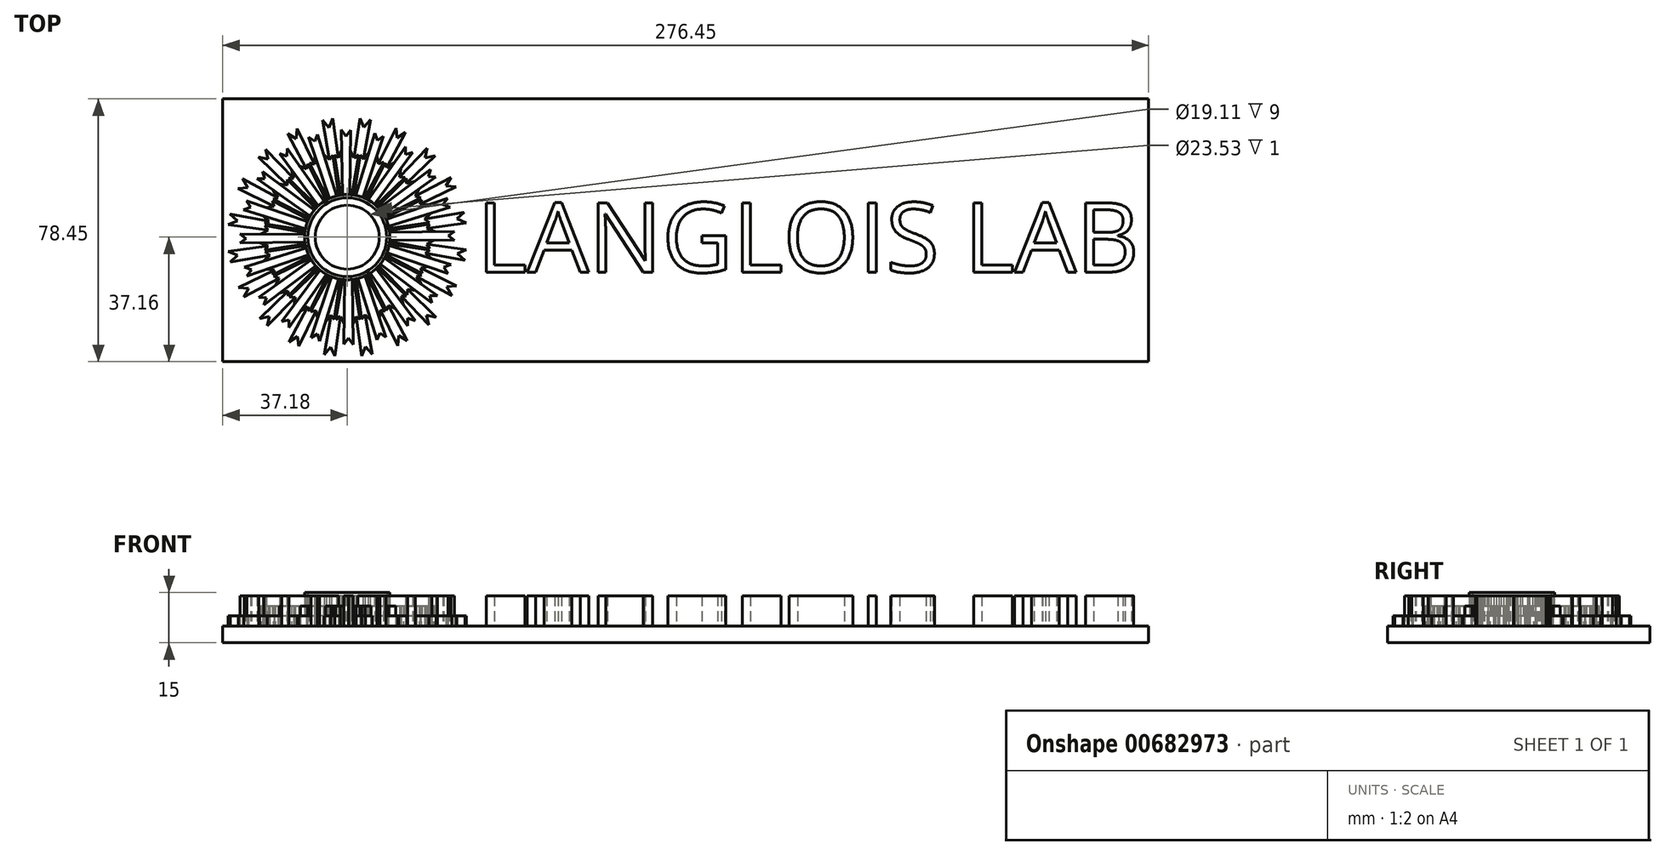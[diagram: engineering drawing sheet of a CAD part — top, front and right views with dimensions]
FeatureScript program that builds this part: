
annotation { "Feature Type Name" : "Feature", "Feature Type Description" : "" }
export const myFeature = defineFeature(function(context is Context, id is Id, definition is map)
    precondition{}
    {
        {
            var Q0;
            Q0=qCreatedBy(makeId("Top.planeOp"),FACE);
            var sketch = newSketch(context, id + "F0", { "sketchPlane" : qUnion([Q0])});
            skCircle(sketch, "E0", {"center": v(0, 0) * mm, "radius": 9.55 * mm});
            skCircle(sketch, "E1", {"center": v(0, 0) * mm, "radius": 11.77 * mm});
            skCircle(sketch, "E2", {"center": v(0, 0) * mm, "radius": 12.74 * mm});
            skLineSegment(sketch, "E3", {"start": v(-8.1, -9.83) * mm, "end": v(-19.6, -25.28) * mm});
            skLineSegment(sketch, "E4", {"start": v(-19.6, -25.28) * mm, "end": v(-17.42, -24.67) * mm});
            skLineSegment(sketch, "E5", {"start": v(-17.42, -24.67) * mm, "end": v(-17.42, -26.96) * mm});
            skLineSegment(sketch, "E6", {"start": v(-17.42, -26.96) * mm, "end": v(-6.24, -11.1) * mm});
            skLineSegment(sketch, "E7.1.0", {"start": v(-8.24, -31.02) * mm, "end": v(-2.5, -12.49) * mm});
            skLineSegment(sketch, "E7.1.1", {"start": v(-8.95, -28.84) * mm, "end": v(-8.24, -31.02) * mm});
            skLineSegment(sketch, "E7.1.2", {"start": v(-10.83, -30.1) * mm, "end": v(-8.95, -28.84) * mm});
            skLineSegment(sketch, "E7.1.3", {"start": v(-4.67, -11.85) * mm, "end": v(-10.83, -30.1) * mm});
            skLineSegment(sketch, "E7.2.0", {"start": v(1.75, -32.05) * mm, "end": v(1.47, -12.65) * mm});
            skLineSegment(sketch, "E7.2.1", {"start": v(0.4, -30.2) * mm, "end": v(1.75, -32.05) * mm});
            skLineSegment(sketch, "E7.2.2", {"start": v(-1, -31.97) * mm, "end": v(0.4, -30.2) * mm});
            skLineSegment(sketch, "E7.2.3", {"start": v(-0.77, -12.71) * mm, "end": v(-1, -31.97) * mm});
            skLineSegment(sketch, "E7.3.0", {"start": v(11.57, -29.94) * mm, "end": v(5.31, -11.58) * mm});
            skLineSegment(sketch, "E7.3.1", {"start": v(9.71, -28.6) * mm, "end": v(11.57, -29.94) * mm});
            skLineSegment(sketch, "E7.3.2", {"start": v(8.93, -30.71) * mm, "end": v(9.71, -28.6) * mm});
            skLineSegment(sketch, "E7.3.3", {"start": v(3.2, -12.33) * mm, "end": v(8.93, -30.71) * mm});
            skLineSegment(sketch, "E7.4.0", {"start": v(20.25, -24.9) * mm, "end": v(8.63, -9.37) * mm});
            skLineSegment(sketch, "E7.4.1", {"start": v(18.08, -24.2) * mm, "end": v(20.25, -24.9) * mm});
            skLineSegment(sketch, "E7.4.2", {"start": v(17.98, -26.45) * mm, "end": v(18.08, -24.2) * mm});
            skLineSegment(sketch, "E7.4.3", {"start": v(6.85, -10.74) * mm, "end": v(17.98, -26.45) * mm});
            skLineSegment(sketch, "E7.5.0", {"start": v(26.96, -17.42) * mm, "end": v(11.1, -6.24) * mm});
            skLineSegment(sketch, "E7.5.1", {"start": v(24.67, -17.42) * mm, "end": v(26.96, -17.42) * mm});
            skLineSegment(sketch, "E7.5.2", {"start": v(25.28, -19.6) * mm, "end": v(24.67, -17.42) * mm});
            skLineSegment(sketch, "E7.5.3", {"start": v(9.83, -8.1) * mm, "end": v(25.28, -19.6) * mm});
            skLineSegment(sketch, "E7.6.0", {"start": v(31.02, -8.24) * mm, "end": v(12.49, -2.5) * mm});
            skLineSegment(sketch, "E7.6.1", {"start": v(28.84, -8.95) * mm, "end": v(31.02, -8.24) * mm});
            skLineSegment(sketch, "E7.6.2", {"start": v(30.1, -10.83) * mm, "end": v(28.84, -8.95) * mm});
            skLineSegment(sketch, "E7.6.3", {"start": v(11.85, -4.67) * mm, "end": v(30.1, -10.83) * mm});
            skLineSegment(sketch, "E7.7.0", {"start": v(32.05, 1.75) * mm, "end": v(12.65, 1.47) * mm});
            skLineSegment(sketch, "E7.7.1", {"start": v(30.2, 0.4) * mm, "end": v(32.05, 1.75) * mm});
            skLineSegment(sketch, "E7.7.2", {"start": v(31.97, -1) * mm, "end": v(30.2, 0.4) * mm});
            skLineSegment(sketch, "E7.7.3", {"start": v(12.71, -0.77) * mm, "end": v(31.97, -1) * mm});
            skLineSegment(sketch, "E7.8.0", {"start": v(29.94, 11.57) * mm, "end": v(11.58, 5.31) * mm});
            skLineSegment(sketch, "E7.8.1", {"start": v(28.6, 9.71) * mm, "end": v(29.94, 11.57) * mm});
            skLineSegment(sketch, "E7.8.2", {"start": v(30.71, 8.93) * mm, "end": v(28.6, 9.71) * mm});
            skLineSegment(sketch, "E7.8.3", {"start": v(12.33, 3.2) * mm, "end": v(30.71, 8.93) * mm});
            skLineSegment(sketch, "E7.9.0", {"start": v(24.9, 20.25) * mm, "end": v(9.37, 8.63) * mm});
            skLineSegment(sketch, "E7.9.1", {"start": v(24.2, 18.08) * mm, "end": v(24.9, 20.25) * mm});
            skLineSegment(sketch, "E7.9.2", {"start": v(26.45, 17.98) * mm, "end": v(24.2, 18.08) * mm});
            skLineSegment(sketch, "E7.9.3", {"start": v(10.74, 6.85) * mm, "end": v(26.45, 17.98) * mm});
            skLineSegment(sketch, "E7.10.0", {"start": v(17.42, 26.96) * mm, "end": v(6.24, 11.1) * mm});
            skLineSegment(sketch, "E7.10.1", {"start": v(17.42, 24.67) * mm, "end": v(17.42, 26.96) * mm});
            skLineSegment(sketch, "E7.10.2", {"start": v(19.6, 25.28) * mm, "end": v(17.42, 24.67) * mm});
            skLineSegment(sketch, "E7.10.3", {"start": v(8.1, 9.83) * mm, "end": v(19.6, 25.28) * mm});
            skLineSegment(sketch, "E7.11.0", {"start": v(8.24, 31.02) * mm, "end": v(2.5, 12.49) * mm});
            skLineSegment(sketch, "E7.11.1", {"start": v(8.95, 28.84) * mm, "end": v(8.24, 31.02) * mm});
            skLineSegment(sketch, "E7.11.2", {"start": v(10.83, 30.1) * mm, "end": v(8.95, 28.84) * mm});
            skLineSegment(sketch, "E7.11.3", {"start": v(4.67, 11.85) * mm, "end": v(10.83, 30.1) * mm});
            skLineSegment(sketch, "E7.12.0", {"start": v(-1.75, 32.05) * mm, "end": v(-1.47, 12.65) * mm});
            skLineSegment(sketch, "E7.12.1", {"start": v(-0.4, 30.2) * mm, "end": v(-1.75, 32.05) * mm});
            skLineSegment(sketch, "E7.12.2", {"start": v(1, 31.97) * mm, "end": v(-0.4, 30.2) * mm});
            skLineSegment(sketch, "E7.12.3", {"start": v(0.77, 12.71) * mm, "end": v(1, 31.97) * mm});
            skLineSegment(sketch, "E7.13.0", {"start": v(-11.57, 29.94) * mm, "end": v(-5.31, 11.58) * mm});
            skLineSegment(sketch, "E7.13.1", {"start": v(-9.71, 28.6) * mm, "end": v(-11.57, 29.94) * mm});
            skLineSegment(sketch, "E7.13.2", {"start": v(-8.93, 30.71) * mm, "end": v(-9.71, 28.6) * mm});
            skLineSegment(sketch, "E7.13.3", {"start": v(-3.2, 12.33) * mm, "end": v(-8.93, 30.71) * mm});
            skLineSegment(sketch, "E7.14.0", {"start": v(-20.25, 24.9) * mm, "end": v(-8.63, 9.37) * mm});
            skLineSegment(sketch, "E7.14.1", {"start": v(-18.08, 24.2) * mm, "end": v(-20.25, 24.9) * mm});
            skLineSegment(sketch, "E7.14.2", {"start": v(-17.98, 26.45) * mm, "end": v(-18.08, 24.2) * mm});
            skLineSegment(sketch, "E7.14.3", {"start": v(-6.85, 10.74) * mm, "end": v(-17.98, 26.45) * mm});
            skLineSegment(sketch, "E7.15.0", {"start": v(-26.96, 17.42) * mm, "end": v(-11.1, 6.24) * mm});
            skLineSegment(sketch, "E7.15.1", {"start": v(-24.67, 17.42) * mm, "end": v(-26.96, 17.42) * mm});
            skLineSegment(sketch, "E7.15.2", {"start": v(-25.28, 19.6) * mm, "end": v(-24.67, 17.42) * mm});
            skLineSegment(sketch, "E7.15.3", {"start": v(-9.83, 8.1) * mm, "end": v(-25.28, 19.6) * mm});
            skLineSegment(sketch, "E7.16.0", {"start": v(-31.02, 8.24) * mm, "end": v(-12.49, 2.5) * mm});
            skLineSegment(sketch, "E7.16.1", {"start": v(-28.84, 8.95) * mm, "end": v(-31.02, 8.24) * mm});
            skLineSegment(sketch, "E7.16.2", {"start": v(-30.1, 10.83) * mm, "end": v(-28.84, 8.95) * mm});
            skLineSegment(sketch, "E7.16.3", {"start": v(-11.85, 4.67) * mm, "end": v(-30.1, 10.83) * mm});
            skLineSegment(sketch, "E7.17.0", {"start": v(-32.05, -1.75) * mm, "end": v(-12.65, -1.47) * mm});
            skLineSegment(sketch, "E7.17.1", {"start": v(-30.2, -0.4) * mm, "end": v(-32.05, -1.75) * mm});
            skLineSegment(sketch, "E7.17.2", {"start": v(-31.97, 1) * mm, "end": v(-30.2, -0.4) * mm});
            skLineSegment(sketch, "E7.17.3", {"start": v(-12.71, 0.77) * mm, "end": v(-31.97, 1) * mm});
            skLineSegment(sketch, "E7.18.0", {"start": v(-29.94, -11.57) * mm, "end": v(-11.58, -5.31) * mm});
            skLineSegment(sketch, "E7.18.1", {"start": v(-28.6, -9.71) * mm, "end": v(-29.94, -11.57) * mm});
            skLineSegment(sketch, "E7.18.2", {"start": v(-30.71, -8.93) * mm, "end": v(-28.6, -9.71) * mm});
            skLineSegment(sketch, "E7.18.3", {"start": v(-12.33, -3.2) * mm, "end": v(-30.71, -8.93) * mm});
            skLineSegment(sketch, "E7.19.0", {"start": v(-24.9, -20.25) * mm, "end": v(-9.37, -8.63) * mm});
            skLineSegment(sketch, "E7.19.1", {"start": v(-24.2, -18.08) * mm, "end": v(-24.9, -20.25) * mm});
            skLineSegment(sketch, "E7.19.2", {"start": v(-26.45, -17.98) * mm, "end": v(-24.2, -18.08) * mm});
            skLineSegment(sketch, "E7.19.3", {"start": v(-10.74, -6.85) * mm, "end": v(-26.45, -17.98) * mm});
            skLineSegment(sketch, "E8", {"start": v(-14, -22.1) * mm, "end": v(-11.8, -20.73) * mm});
            skLineSegment(sketch, "E9", {"start": v(-11.8, -20.73) * mm, "end": v(-11.35, -22.17) * mm});
            skLineSegment(sketch, "E10", {"start": v(-11.35, -22.17) * mm, "end": v(-5.84, -11.32) * mm});
            skLineSegment(sketch, "E11", {"start": v(-5.22, -11.62) * mm, "end": v(-10.89, -22.36) * mm});
            skLineSegment(sketch, "E12", {"start": v(-10.89, -22.36) * mm, "end": v(-9.26, -21.9) * mm});
            skLineSegment(sketch, "E13", {"start": v(-9.26, -21.9) * mm, "end": v(-8.86, -24.28) * mm});
            skLineSegment(sketch, "E14", {"start": v(-11.8, -20.73) * mm, "end": v(-17.42, -31.26) * mm});
            skLineSegment(sketch, "E15", {"start": v(-17.42, -31.26) * mm, "end": v(-14.82, -29.7) * mm});
            skLineSegment(sketch, "E16", {"start": v(-14.82, -29.7) * mm, "end": v(-14.53, -32.63) * mm});
            skLineSegment(sketch, "E17", {"start": v(-14.53, -32.63) * mm, "end": v(-9.26, -21.9) * mm});
            skLineSegment(sketch, "E18.1.0", {"start": v(-6.49, -25.35) * mm, "end": v(-4.81, -23.36) * mm});
            skLineSegment(sketch, "E18.1.1", {"start": v(-4.81, -23.36) * mm, "end": v(-6.91, -35.11) * mm});
            skLineSegment(sketch, "E18.1.2", {"start": v(-4.81, -23.36) * mm, "end": v(-3.94, -24.6) * mm});
            skLineSegment(sketch, "E18.1.3", {"start": v(-3.94, -24.6) * mm, "end": v(-2.05, -12.57) * mm});
            skLineSegment(sketch, "E18.1.4", {"start": v(-3.74, -35.52) * mm, "end": v(-2.04, -23.68) * mm});
            skLineSegment(sketch, "E18.1.5", {"start": v(-3.45, -24.63) * mm, "end": v(-2.04, -23.68) * mm});
            skLineSegment(sketch, "E18.1.6", {"start": v(-1.37, -12.66) * mm, "end": v(-3.45, -24.63) * mm});
            skLineSegment(sketch, "E18.1.7", {"start": v(-2.04, -23.68) * mm, "end": v(-0.93, -25.83) * mm});
            skLineSegment(sketch, "E18.1.8", {"start": v(-4.92, -32.82) * mm, "end": v(-3.74, -35.52) * mm});
            skLineSegment(sketch, "E18.1.9", {"start": v(-6.91, -35.11) * mm, "end": v(-4.92, -32.82) * mm});
            skLineSegment(sketch, "E18.2.0", {"start": v(1.67, -26.11) * mm, "end": v(2.64, -23.7) * mm});
            skLineSegment(sketch, "E18.2.1", {"start": v(2.64, -23.7) * mm, "end": v(4.28, -35.53) * mm});
            skLineSegment(sketch, "E18.2.2", {"start": v(2.64, -23.7) * mm, "end": v(3.85, -24.6) * mm});
            skLineSegment(sketch, "E18.2.3", {"start": v(3.85, -24.6) * mm, "end": v(1.93, -12.59) * mm});
            skLineSegment(sketch, "E18.2.4", {"start": v(7.42, -34.94) * mm, "end": v(5.38, -23.16) * mm});
            skLineSegment(sketch, "E18.2.5", {"start": v(4.33, -24.49) * mm, "end": v(5.38, -23.16) * mm});
            skLineSegment(sketch, "E18.2.6", {"start": v(2.6, -12.47) * mm, "end": v(4.33, -24.49) * mm});
            skLineSegment(sketch, "E18.2.7", {"start": v(5.38, -23.16) * mm, "end": v(7.1, -24.85) * mm});
            skLineSegment(sketch, "E18.2.8", {"start": v(5.47, -32.74) * mm, "end": v(7.42, -34.94) * mm});
            skLineSegment(sketch, "E18.2.9", {"start": v(4.28, -35.53) * mm, "end": v(5.47, -32.74) * mm});
            skLineSegment(sketch, "E18.3.0", {"start": v(9.65, -24.32) * mm, "end": v(9.84, -21.72) * mm});
            skLineSegment(sketch, "E18.3.1", {"start": v(9.84, -21.72) * mm, "end": v(15.05, -32.47) * mm});
            skLineSegment(sketch, "E18.3.2", {"start": v(9.84, -21.72) * mm, "end": v(11.27, -22.21) * mm});
            skLineSegment(sketch, "E18.3.3", {"start": v(11.27, -22.21) * mm, "end": v(5.73, -11.38) * mm});
            skLineSegment(sketch, "E18.3.4", {"start": v(17.85, -30.93) * mm, "end": v(12.27, -20.36) * mm});
            skLineSegment(sketch, "E18.3.5", {"start": v(11.69, -21.95) * mm, "end": v(12.27, -20.36) * mm});
            skLineSegment(sketch, "E18.3.6", {"start": v(6.33, -11.05) * mm, "end": v(11.69, -21.95) * mm});
            skLineSegment(sketch, "E18.3.7", {"start": v(12.27, -20.36) * mm, "end": v(14.43, -21.44) * mm});
            skLineSegment(sketch, "E18.3.8", {"start": v(15.31, -29.45) * mm, "end": v(17.85, -30.93) * mm});
            skLineSegment(sketch, "E18.3.9", {"start": v(15.05, -32.47) * mm, "end": v(15.31, -29.45) * mm});
            skLineSegment(sketch, "E18.4.0", {"start": v(16.7, -20.15) * mm, "end": v(16.07, -17.62) * mm});
            skLineSegment(sketch, "E18.4.1", {"start": v(16.07, -17.62) * mm, "end": v(24.34, -26.23) * mm});
            skLineSegment(sketch, "E18.4.2", {"start": v(16.07, -17.62) * mm, "end": v(17.58, -17.64) * mm});
            skLineSegment(sketch, "E18.4.3", {"start": v(17.58, -17.64) * mm, "end": v(8.96, -9.05) * mm});
            skLineSegment(sketch, "E18.4.4", {"start": v(26.54, -23.9) * mm, "end": v(17.96, -15.57) * mm});
            skLineSegment(sketch, "E18.4.5", {"start": v(17.9, -17.27) * mm, "end": v(17.96, -15.57) * mm});
            skLineSegment(sketch, "E18.4.6", {"start": v(9.44, -8.55) * mm, "end": v(17.9, -17.27) * mm});
            skLineSegment(sketch, "E18.4.7", {"start": v(17.96, -15.57) * mm, "end": v(20.35, -15.93) * mm});
            skLineSegment(sketch, "E18.4.8", {"start": v(23.66, -23.27) * mm, "end": v(26.54, -23.9) * mm});
            skLineSegment(sketch, "E18.4.9", {"start": v(24.34, -26.23) * mm, "end": v(23.66, -23.27) * mm});
            skLineSegment(sketch, "E18.5.0", {"start": v(22.1, -14) * mm, "end": v(20.73, -11.8) * mm});
            skLineSegment(sketch, "E18.5.1", {"start": v(20.73, -11.8) * mm, "end": v(31.26, -17.42) * mm});
            skLineSegment(sketch, "E18.5.2", {"start": v(20.73, -11.8) * mm, "end": v(22.17, -11.35) * mm});
            skLineSegment(sketch, "E18.5.3", {"start": v(22.17, -11.35) * mm, "end": v(11.32, -5.84) * mm});
            skLineSegment(sketch, "E18.5.4", {"start": v(32.63, -14.53) * mm, "end": v(21.9, -9.26) * mm});
            skLineSegment(sketch, "E18.5.5", {"start": v(22.36, -10.89) * mm, "end": v(21.9, -9.26) * mm});
            skLineSegment(sketch, "E18.5.6", {"start": v(11.62, -5.22) * mm, "end": v(22.36, -10.89) * mm});
            skLineSegment(sketch, "E18.5.7", {"start": v(21.9, -9.26) * mm, "end": v(24.28, -8.86) * mm});
            skLineSegment(sketch, "E18.5.8", {"start": v(29.7, -14.82) * mm, "end": v(32.63, -14.53) * mm});
            skLineSegment(sketch, "E18.5.9", {"start": v(31.26, -17.42) * mm, "end": v(29.7, -14.82) * mm});
            skLineSegment(sketch, "E18.6.0", {"start": v(25.35, -6.49) * mm, "end": v(23.36, -4.81) * mm});
            skLineSegment(sketch, "E18.6.1", {"start": v(23.36, -4.81) * mm, "end": v(35.11, -6.91) * mm});
            skLineSegment(sketch, "E18.6.2", {"start": v(23.36, -4.81) * mm, "end": v(24.6, -3.94) * mm});
            skLineSegment(sketch, "E18.6.3", {"start": v(24.6, -3.94) * mm, "end": v(12.57, -2.05) * mm});
            skLineSegment(sketch, "E18.6.4", {"start": v(35.52, -3.74) * mm, "end": v(23.68, -2.04) * mm});
            skLineSegment(sketch, "E18.6.5", {"start": v(24.63, -3.45) * mm, "end": v(23.68, -2.04) * mm});
            skLineSegment(sketch, "E18.6.6", {"start": v(12.66, -1.37) * mm, "end": v(24.63, -3.45) * mm});
            skLineSegment(sketch, "E18.6.7", {"start": v(23.68, -2.04) * mm, "end": v(25.83, -0.93) * mm});
            skLineSegment(sketch, "E18.6.8", {"start": v(32.82, -4.92) * mm, "end": v(35.52, -3.74) * mm});
            skLineSegment(sketch, "E18.6.9", {"start": v(35.11, -6.91) * mm, "end": v(32.82, -4.92) * mm});
            skLineSegment(sketch, "E18.7.0", {"start": v(26.11, 1.67) * mm, "end": v(23.7, 2.64) * mm});
            skLineSegment(sketch, "E18.7.1", {"start": v(23.7, 2.64) * mm, "end": v(35.53, 4.28) * mm});
            skLineSegment(sketch, "E18.7.2", {"start": v(23.7, 2.64) * mm, "end": v(24.6, 3.85) * mm});
            skLineSegment(sketch, "E18.7.3", {"start": v(24.6, 3.85) * mm, "end": v(12.59, 1.93) * mm});
            skLineSegment(sketch, "E18.7.4", {"start": v(34.94, 7.42) * mm, "end": v(23.16, 5.38) * mm});
            skLineSegment(sketch, "E18.7.5", {"start": v(24.49, 4.33) * mm, "end": v(23.16, 5.38) * mm});
            skLineSegment(sketch, "E18.7.6", {"start": v(12.47, 2.6) * mm, "end": v(24.49, 4.33) * mm});
            skLineSegment(sketch, "E18.7.7", {"start": v(23.16, 5.38) * mm, "end": v(24.85, 7.1) * mm});
            skLineSegment(sketch, "E18.7.8", {"start": v(32.74, 5.47) * mm, "end": v(34.94, 7.42) * mm});
            skLineSegment(sketch, "E18.7.9", {"start": v(35.53, 4.28) * mm, "end": v(32.74, 5.47) * mm});
            skLineSegment(sketch, "E18.8.0", {"start": v(24.32, 9.65) * mm, "end": v(21.72, 9.84) * mm});
            skLineSegment(sketch, "E18.8.1", {"start": v(21.72, 9.84) * mm, "end": v(32.47, 15.05) * mm});
            skLineSegment(sketch, "E18.8.2", {"start": v(21.72, 9.84) * mm, "end": v(22.21, 11.27) * mm});
            skLineSegment(sketch, "E18.8.3", {"start": v(22.21, 11.27) * mm, "end": v(11.38, 5.73) * mm});
            skLineSegment(sketch, "E18.8.4", {"start": v(30.93, 17.85) * mm, "end": v(20.36, 12.27) * mm});
            skLineSegment(sketch, "E18.8.5", {"start": v(21.95, 11.69) * mm, "end": v(20.36, 12.27) * mm});
            skLineSegment(sketch, "E18.8.6", {"start": v(11.05, 6.33) * mm, "end": v(21.95, 11.69) * mm});
            skLineSegment(sketch, "E18.8.7", {"start": v(20.36, 12.27) * mm, "end": v(21.44, 14.43) * mm});
            skLineSegment(sketch, "E18.8.8", {"start": v(29.45, 15.31) * mm, "end": v(30.93, 17.85) * mm});
            skLineSegment(sketch, "E18.8.9", {"start": v(32.47, 15.05) * mm, "end": v(29.45, 15.31) * mm});
            skLineSegment(sketch, "E18.9.0", {"start": v(20.15, 16.7) * mm, "end": v(17.62, 16.07) * mm});
            skLineSegment(sketch, "E18.9.1", {"start": v(17.62, 16.07) * mm, "end": v(26.23, 24.34) * mm});
            skLineSegment(sketch, "E18.9.2", {"start": v(17.62, 16.07) * mm, "end": v(17.64, 17.58) * mm});
            skLineSegment(sketch, "E18.9.3", {"start": v(17.64, 17.58) * mm, "end": v(9.05, 8.96) * mm});
            skLineSegment(sketch, "E18.9.4", {"start": v(23.9, 26.54) * mm, "end": v(15.57, 17.96) * mm});
            skLineSegment(sketch, "E18.9.5", {"start": v(17.27, 17.9) * mm, "end": v(15.57, 17.96) * mm});
            skLineSegment(sketch, "E18.9.6", {"start": v(8.55, 9.44) * mm, "end": v(17.27, 17.9) * mm});
            skLineSegment(sketch, "E18.9.7", {"start": v(15.57, 17.96) * mm, "end": v(15.93, 20.35) * mm});
            skLineSegment(sketch, "E18.9.8", {"start": v(23.27, 23.66) * mm, "end": v(23.9, 26.54) * mm});
            skLineSegment(sketch, "E18.9.9", {"start": v(26.23, 24.34) * mm, "end": v(23.27, 23.66) * mm});
            skLineSegment(sketch, "E18.10.0", {"start": v(14, 22.1) * mm, "end": v(11.8, 20.73) * mm});
            skLineSegment(sketch, "E18.10.1", {"start": v(11.8, 20.73) * mm, "end": v(17.42, 31.26) * mm});
            skLineSegment(sketch, "E18.10.2", {"start": v(11.8, 20.73) * mm, "end": v(11.35, 22.17) * mm});
            skLineSegment(sketch, "E18.10.3", {"start": v(11.35, 22.17) * mm, "end": v(5.84, 11.32) * mm});
            skLineSegment(sketch, "E18.10.4", {"start": v(14.53, 32.63) * mm, "end": v(9.26, 21.9) * mm});
            skLineSegment(sketch, "E18.10.5", {"start": v(10.89, 22.36) * mm, "end": v(9.26, 21.9) * mm});
            skLineSegment(sketch, "E18.10.6", {"start": v(5.22, 11.62) * mm, "end": v(10.89, 22.36) * mm});
            skLineSegment(sketch, "E18.10.7", {"start": v(9.26, 21.9) * mm, "end": v(8.86, 24.28) * mm});
            skLineSegment(sketch, "E18.10.8", {"start": v(14.82, 29.7) * mm, "end": v(14.53, 32.63) * mm});
            skLineSegment(sketch, "E18.10.9", {"start": v(17.42, 31.26) * mm, "end": v(14.82, 29.7) * mm});
            skLineSegment(sketch, "E18.11.0", {"start": v(6.49, 25.35) * mm, "end": v(4.81, 23.36) * mm});
            skLineSegment(sketch, "E18.11.1", {"start": v(4.81, 23.36) * mm, "end": v(6.91, 35.11) * mm});
            skLineSegment(sketch, "E18.11.2", {"start": v(4.81, 23.36) * mm, "end": v(3.94, 24.6) * mm});
            skLineSegment(sketch, "E18.11.3", {"start": v(3.94, 24.6) * mm, "end": v(2.05, 12.57) * mm});
            skLineSegment(sketch, "E18.11.4", {"start": v(3.74, 35.52) * mm, "end": v(2.04, 23.68) * mm});
            skLineSegment(sketch, "E18.11.5", {"start": v(3.45, 24.63) * mm, "end": v(2.04, 23.68) * mm});
            skLineSegment(sketch, "E18.11.6", {"start": v(1.37, 12.66) * mm, "end": v(3.45, 24.63) * mm});
            skLineSegment(sketch, "E18.11.7", {"start": v(2.04, 23.68) * mm, "end": v(0.93, 25.83) * mm});
            skLineSegment(sketch, "E18.11.8", {"start": v(4.92, 32.82) * mm, "end": v(3.74, 35.52) * mm});
            skLineSegment(sketch, "E18.11.9", {"start": v(6.91, 35.11) * mm, "end": v(4.92, 32.82) * mm});
            skLineSegment(sketch, "E18.12.0", {"start": v(-1.67, 26.11) * mm, "end": v(-2.64, 23.7) * mm});
            skLineSegment(sketch, "E18.12.1", {"start": v(-2.64, 23.7) * mm, "end": v(-4.28, 35.53) * mm});
            skLineSegment(sketch, "E18.12.2", {"start": v(-2.64, 23.7) * mm, "end": v(-3.85, 24.6) * mm});
            skLineSegment(sketch, "E18.12.3", {"start": v(-3.85, 24.6) * mm, "end": v(-1.93, 12.59) * mm});
            skLineSegment(sketch, "E18.12.4", {"start": v(-7.42, 34.94) * mm, "end": v(-5.38, 23.16) * mm});
            skLineSegment(sketch, "E18.12.5", {"start": v(-4.33, 24.49) * mm, "end": v(-5.38, 23.16) * mm});
            skLineSegment(sketch, "E18.12.6", {"start": v(-2.6, 12.47) * mm, "end": v(-4.33, 24.49) * mm});
            skLineSegment(sketch, "E18.12.7", {"start": v(-5.38, 23.16) * mm, "end": v(-7.1, 24.85) * mm});
            skLineSegment(sketch, "E18.12.8", {"start": v(-5.47, 32.74) * mm, "end": v(-7.42, 34.94) * mm});
            skLineSegment(sketch, "E18.12.9", {"start": v(-4.28, 35.53) * mm, "end": v(-5.47, 32.74) * mm});
            skLineSegment(sketch, "E18.13.0", {"start": v(-9.65, 24.32) * mm, "end": v(-9.84, 21.72) * mm});
            skLineSegment(sketch, "E18.13.1", {"start": v(-9.84, 21.72) * mm, "end": v(-15.05, 32.47) * mm});
            skLineSegment(sketch, "E18.13.2", {"start": v(-9.84, 21.72) * mm, "end": v(-11.27, 22.21) * mm});
            skLineSegment(sketch, "E18.13.3", {"start": v(-11.27, 22.21) * mm, "end": v(-5.73, 11.38) * mm});
            skLineSegment(sketch, "E18.13.4", {"start": v(-17.85, 30.93) * mm, "end": v(-12.27, 20.36) * mm});
            skLineSegment(sketch, "E18.13.5", {"start": v(-11.69, 21.95) * mm, "end": v(-12.27, 20.36) * mm});
            skLineSegment(sketch, "E18.13.6", {"start": v(-6.33, 11.05) * mm, "end": v(-11.69, 21.95) * mm});
            skLineSegment(sketch, "E18.13.7", {"start": v(-12.27, 20.36) * mm, "end": v(-14.43, 21.44) * mm});
            skLineSegment(sketch, "E18.13.8", {"start": v(-15.31, 29.45) * mm, "end": v(-17.85, 30.93) * mm});
            skLineSegment(sketch, "E18.13.9", {"start": v(-15.05, 32.47) * mm, "end": v(-15.31, 29.45) * mm});
            skLineSegment(sketch, "E18.14.0", {"start": v(-16.7, 20.15) * mm, "end": v(-16.07, 17.62) * mm});
            skLineSegment(sketch, "E18.14.1", {"start": v(-16.07, 17.62) * mm, "end": v(-24.34, 26.23) * mm});
            skLineSegment(sketch, "E18.14.2", {"start": v(-16.07, 17.62) * mm, "end": v(-17.58, 17.64) * mm});
            skLineSegment(sketch, "E18.14.3", {"start": v(-17.58, 17.64) * mm, "end": v(-8.96, 9.05) * mm});
            skLineSegment(sketch, "E18.14.4", {"start": v(-26.54, 23.9) * mm, "end": v(-17.96, 15.57) * mm});
            skLineSegment(sketch, "E18.14.5", {"start": v(-17.9, 17.27) * mm, "end": v(-17.96, 15.57) * mm});
            skLineSegment(sketch, "E18.14.6", {"start": v(-9.44, 8.55) * mm, "end": v(-17.9, 17.27) * mm});
            skLineSegment(sketch, "E18.14.7", {"start": v(-17.96, 15.57) * mm, "end": v(-20.35, 15.93) * mm});
            skLineSegment(sketch, "E18.14.8", {"start": v(-23.66, 23.27) * mm, "end": v(-26.54, 23.9) * mm});
            skLineSegment(sketch, "E18.14.9", {"start": v(-24.34, 26.23) * mm, "end": v(-23.66, 23.27) * mm});
            skLineSegment(sketch, "E18.15.0", {"start": v(-22.1, 14) * mm, "end": v(-20.73, 11.8) * mm});
            skLineSegment(sketch, "E18.15.1", {"start": v(-20.73, 11.8) * mm, "end": v(-31.26, 17.42) * mm});
            skLineSegment(sketch, "E18.15.2", {"start": v(-20.73, 11.8) * mm, "end": v(-22.17, 11.35) * mm});
            skLineSegment(sketch, "E18.15.3", {"start": v(-22.17, 11.35) * mm, "end": v(-11.32, 5.84) * mm});
            skLineSegment(sketch, "E18.15.4", {"start": v(-32.63, 14.53) * mm, "end": v(-21.9, 9.26) * mm});
            skLineSegment(sketch, "E18.15.5", {"start": v(-22.36, 10.89) * mm, "end": v(-21.9, 9.26) * mm});
            skLineSegment(sketch, "E18.15.6", {"start": v(-11.62, 5.22) * mm, "end": v(-22.36, 10.89) * mm});
            skLineSegment(sketch, "E18.15.7", {"start": v(-21.9, 9.26) * mm, "end": v(-24.28, 8.86) * mm});
            skLineSegment(sketch, "E18.15.8", {"start": v(-29.7, 14.82) * mm, "end": v(-32.63, 14.53) * mm});
            skLineSegment(sketch, "E18.15.9", {"start": v(-31.26, 17.42) * mm, "end": v(-29.7, 14.82) * mm});
            skLineSegment(sketch, "E18.16.0", {"start": v(-25.35, 6.49) * mm, "end": v(-23.36, 4.81) * mm});
            skLineSegment(sketch, "E18.16.1", {"start": v(-23.36, 4.81) * mm, "end": v(-35.11, 6.91) * mm});
            skLineSegment(sketch, "E18.16.2", {"start": v(-23.36, 4.81) * mm, "end": v(-24.6, 3.94) * mm});
            skLineSegment(sketch, "E18.16.3", {"start": v(-24.6, 3.94) * mm, "end": v(-12.57, 2.05) * mm});
            skLineSegment(sketch, "E18.16.4", {"start": v(-35.52, 3.74) * mm, "end": v(-23.68, 2.04) * mm});
            skLineSegment(sketch, "E18.16.5", {"start": v(-24.63, 3.45) * mm, "end": v(-23.68, 2.04) * mm});
            skLineSegment(sketch, "E18.16.6", {"start": v(-12.66, 1.37) * mm, "end": v(-24.63, 3.45) * mm});
            skLineSegment(sketch, "E18.16.7", {"start": v(-23.68, 2.04) * mm, "end": v(-25.83, 0.93) * mm});
            skLineSegment(sketch, "E18.16.8", {"start": v(-32.82, 4.92) * mm, "end": v(-35.52, 3.74) * mm});
            skLineSegment(sketch, "E18.16.9", {"start": v(-35.11, 6.91) * mm, "end": v(-32.82, 4.92) * mm});
            skLineSegment(sketch, "E18.17.0", {"start": v(-26.11, -1.67) * mm, "end": v(-23.7, -2.64) * mm});
            skLineSegment(sketch, "E18.17.1", {"start": v(-23.7, -2.64) * mm, "end": v(-35.53, -4.28) * mm});
            skLineSegment(sketch, "E18.17.2", {"start": v(-23.7, -2.64) * mm, "end": v(-24.6, -3.85) * mm});
            skLineSegment(sketch, "E18.17.3", {"start": v(-24.6, -3.85) * mm, "end": v(-12.59, -1.93) * mm});
            skLineSegment(sketch, "E18.17.4", {"start": v(-34.94, -7.42) * mm, "end": v(-23.16, -5.38) * mm});
            skLineSegment(sketch, "E18.17.5", {"start": v(-24.49, -4.33) * mm, "end": v(-23.16, -5.38) * mm});
            skLineSegment(sketch, "E18.17.6", {"start": v(-12.47, -2.6) * mm, "end": v(-24.49, -4.33) * mm});
            skLineSegment(sketch, "E18.17.7", {"start": v(-23.16, -5.38) * mm, "end": v(-24.85, -7.1) * mm});
            skLineSegment(sketch, "E18.17.8", {"start": v(-32.74, -5.47) * mm, "end": v(-34.94, -7.42) * mm});
            skLineSegment(sketch, "E18.17.9", {"start": v(-35.53, -4.28) * mm, "end": v(-32.74, -5.47) * mm});
            skLineSegment(sketch, "E18.18.0", {"start": v(-24.32, -9.65) * mm, "end": v(-21.72, -9.84) * mm});
            skLineSegment(sketch, "E18.18.1", {"start": v(-21.72, -9.84) * mm, "end": v(-32.47, -15.05) * mm});
            skLineSegment(sketch, "E18.18.2", {"start": v(-21.72, -9.84) * mm, "end": v(-22.21, -11.27) * mm});
            skLineSegment(sketch, "E18.18.3", {"start": v(-22.21, -11.27) * mm, "end": v(-11.38, -5.73) * mm});
            skLineSegment(sketch, "E18.18.4", {"start": v(-30.93, -17.85) * mm, "end": v(-20.36, -12.27) * mm});
            skLineSegment(sketch, "E18.18.5", {"start": v(-21.95, -11.69) * mm, "end": v(-20.36, -12.27) * mm});
            skLineSegment(sketch, "E18.18.6", {"start": v(-11.05, -6.33) * mm, "end": v(-21.95, -11.69) * mm});
            skLineSegment(sketch, "E18.18.7", {"start": v(-20.36, -12.27) * mm, "end": v(-21.44, -14.43) * mm});
            skLineSegment(sketch, "E18.18.8", {"start": v(-29.45, -15.31) * mm, "end": v(-30.93, -17.85) * mm});
            skLineSegment(sketch, "E18.18.9", {"start": v(-32.47, -15.05) * mm, "end": v(-29.45, -15.31) * mm});
            skLineSegment(sketch, "E18.19.0", {"start": v(-20.15, -16.7) * mm, "end": v(-17.62, -16.07) * mm});
            skLineSegment(sketch, "E18.19.1", {"start": v(-17.62, -16.07) * mm, "end": v(-26.23, -24.34) * mm});
            skLineSegment(sketch, "E18.19.2", {"start": v(-17.62, -16.07) * mm, "end": v(-17.64, -17.58) * mm});
            skLineSegment(sketch, "E18.19.3", {"start": v(-17.64, -17.58) * mm, "end": v(-9.05, -8.96) * mm});
            skLineSegment(sketch, "E18.19.4", {"start": v(-23.9, -26.54) * mm, "end": v(-15.57, -17.96) * mm});
            skLineSegment(sketch, "E18.19.5", {"start": v(-17.27, -17.9) * mm, "end": v(-15.57, -17.96) * mm});
            skLineSegment(sketch, "E18.19.6", {"start": v(-8.55, -9.44) * mm, "end": v(-17.27, -17.9) * mm});
            skLineSegment(sketch, "E18.19.7", {"start": v(-15.57, -17.96) * mm, "end": v(-15.93, -20.35) * mm});
            skLineSegment(sketch, "E18.19.8", {"start": v(-23.27, -23.66) * mm, "end": v(-23.9, -26.54) * mm});
            skLineSegment(sketch, "E18.19.9", {"start": v(-26.23, -24.34) * mm, "end": v(-23.27, -23.66) * mm});
            skSolve(sketch);
        }
        {
            var Q0;
            Q0=makeQuery(id+"F0.imprint","IMPRINT",FACE,{"disambiguationData":[TD([[makeQuery(id+"F0.imprint","IMPRINT",EDGE,{"derivedFrom":sQuery(id+"F0.wireOp",EDGE,"E0")}),-1.0]])]});
            extrude(context, id + "F1", {"entities" : qUnion([Q0]), "depth" : 9 * mm, "offsetDistance" : 25 * mm});
        }
        {
            var Q0;
            Q0=makeQuery(id+"F0.imprint","IMPRINT",FACE,{"disambiguationData":[TD([[makeQuery(id+"F0.imprint","IMPRINT",EDGE,{"derivedFrom":sQuery(id+"F0.wireOp",EDGE,"E1")}),-1.0]])]});
            extrude(context, id + "F2", {"entities" : qUnion([Q0]), "operationType" : NewBodyOperationType.ADD, "depth" : 10 * mm, "offsetDistance" : 25 * mm});
        }
        {
            var Q0;
            Q0=makeQuery(id+"F0.imprint","IMPRINT",FACE,{"disambiguationData":[TD([[makeQuery(id+"F0.imprint","IMPRINT",EDGE,{"derivedFrom":sQuery(id+"F0.wireOp",EDGE,"E18.3.1")}),1.0]])]});
            var Q1;
            Q1=makeQuery(id+"F0.imprint","IMPRINT",FACE,{"disambiguationData":[TD([[makeQuery(id+"F0.imprint","IMPRINT",EDGE,{"derivedFrom":sQuery(id+"F0.wireOp",EDGE,"E18.4.1")}),1.0]])]});
            var Q2;
            Q2=makeQuery(id+"F0.imprint","IMPRINT",FACE,{"disambiguationData":[TD([[makeQuery(id+"F0.imprint","IMPRINT",EDGE,{"derivedFrom":sQuery(id+"F0.wireOp",EDGE,"E18.5.1")}),1.0]])]});
            var Q3;
            Q3=makeQuery(id+"F0.imprint","IMPRINT",FACE,{"disambiguationData":[TD([[makeQuery(id+"F0.imprint","IMPRINT",EDGE,{"derivedFrom":sQuery(id+"F0.wireOp",EDGE,"E18.6.1")}),1.0]])]});
            var Q4;
            Q4=makeQuery(id+"F0.imprint","IMPRINT",FACE,{"disambiguationData":[TD([[makeQuery(id+"F0.imprint","IMPRINT",EDGE,{"derivedFrom":sQuery(id+"F0.wireOp",EDGE,"E18.7.1")}),1.0]])]});
            var Q5;
            Q5=makeQuery(id+"F0.imprint","IMPRINT",FACE,{"disambiguationData":[TD([[makeQuery(id+"F0.imprint","IMPRINT",EDGE,{"derivedFrom":sQuery(id+"F0.wireOp",EDGE,"E18.8.1")}),1.0]])]});
            var Q6;
            Q6=makeQuery(id+"F0.imprint","IMPRINT",FACE,{"disambiguationData":[TD([[makeQuery(id+"F0.imprint","IMPRINT",EDGE,{"derivedFrom":sQuery(id+"F0.wireOp",EDGE,"E18.9.1")}),1.0]])]});
            var Q7;
            Q7=makeQuery(id+"F0.imprint","IMPRINT",FACE,{"disambiguationData":[TD([[makeQuery(id+"F0.imprint","IMPRINT",EDGE,{"derivedFrom":sQuery(id+"F0.wireOp",EDGE,"E18.10.1")}),1.0]])]});
            var Q8;
            Q8=makeQuery(id+"F0.imprint","IMPRINT",FACE,{"disambiguationData":[TD([[makeQuery(id+"F0.imprint","IMPRINT",EDGE,{"derivedFrom":sQuery(id+"F0.wireOp",EDGE,"E18.11.1")}),1.0]])]});
            var Q9;
            Q9=makeQuery(id+"F0.imprint","IMPRINT",FACE,{"disambiguationData":[TD([[makeQuery(id+"F0.imprint","IMPRINT",EDGE,{"derivedFrom":sQuery(id+"F0.wireOp",EDGE,"E18.12.1")}),1.0]])]});
            var Q10;
            Q10=makeQuery(id+"F0.imprint","IMPRINT",FACE,{"disambiguationData":[TD([[makeQuery(id+"F0.imprint","IMPRINT",EDGE,{"derivedFrom":sQuery(id+"F0.wireOp",EDGE,"E18.13.1")}),1.0]])]});
            var Q11;
            Q11=makeQuery(id+"F0.imprint","IMPRINT",FACE,{"disambiguationData":[TD([[makeQuery(id+"F0.imprint","IMPRINT",EDGE,{"derivedFrom":sQuery(id+"F0.wireOp",EDGE,"E18.14.1")}),1.0]])]});
            var Q12;
            Q12=makeQuery(id+"F0.imprint","IMPRINT",FACE,{"disambiguationData":[TD([[makeQuery(id+"F0.imprint","IMPRINT",EDGE,{"derivedFrom":sQuery(id+"F0.wireOp",EDGE,"E18.15.1")}),1.0]])]});
            var Q13;
            Q13=makeQuery(id+"F0.imprint","IMPRINT",FACE,{"disambiguationData":[TD([[makeQuery(id+"F0.imprint","IMPRINT",EDGE,{"derivedFrom":sQuery(id+"F0.wireOp",EDGE,"E18.16.1")}),1.0]])]});
            var Q14;
            Q14=makeQuery(id+"F0.imprint","IMPRINT",FACE,{"disambiguationData":[TD([[makeQuery(id+"F0.imprint","IMPRINT",EDGE,{"derivedFrom":sQuery(id+"F0.wireOp",EDGE,"E18.17.1")}),1.0]])]});
            var Q15;
            Q15=makeQuery(id+"F0.imprint","IMPRINT",FACE,{"disambiguationData":[TD([[makeQuery(id+"F0.imprint","IMPRINT",EDGE,{"derivedFrom":sQuery(id+"F0.wireOp",EDGE,"E18.18.1")}),1.0]])]});
            var Q16;
            Q16=makeQuery(id+"F0.imprint","IMPRINT",FACE,{"disambiguationData":[TD([[makeQuery(id+"F0.imprint","IMPRINT",EDGE,{"derivedFrom":sQuery(id+"F0.wireOp",EDGE,"E18.19.1")}),1.0]])]});
            var Q17;
            Q17=makeQuery(id+"F0.imprint","IMPRINT",FACE,{"disambiguationData":[TD([[makeQuery(id+"F0.imprint","IMPRINT",EDGE,{"derivedFrom":sQuery(id+"F0.wireOp",EDGE,"E9")}),-1.0]])]});
            var Q18;
            Q18=makeQuery(id+"F0.imprint","IMPRINT",FACE,{"disambiguationData":[TD([[makeQuery(id+"F0.imprint","IMPRINT",EDGE,{"derivedFrom":sQuery(id+"F0.wireOp",EDGE,"E18.1.1")}),1.0]])]});
            var Q19;
            Q19=makeQuery(id+"F0.imprint","IMPRINT",FACE,{"disambiguationData":[TD([[makeQuery(id+"F0.imprint","IMPRINT",EDGE,{"derivedFrom":sQuery(id+"F0.wireOp",EDGE,"E18.2.1")}),1.0]])]});
            extrude(context, id + "F3", {"entities" : qUnion([Q0, Q1, Q2, Q3, Q4, Q5, Q6, Q7, Q8, Q9, Q10, Q11, Q12, Q13, Q14, Q15, Q16, Q17, Q18, Q19]), "operationType" : NewBodyOperationType.ADD, "depth" : 3 * mm, "offsetDistance" : 25 * mm});
        }
        {
            var Q0;
            {var subQ0=sQuery(id+"F0.wireOp",EDGE,"E18.19.0");Q0=makeQuery(id+"F0.imprint","IMPRINT",FACE,{"disambiguationData":[TD([[makeQuery(id+"F0.imprint","IMPRINT",EDGE,{"derivedFrom":subQ0}),1.0]])]});}
            var Q1;
            Q1=makeQuery(id+"F0.imprint","IMPRINT",FACE,{"disambiguationData":[TD([[makeQuery(id+"F0.imprint","IMPRINT",EDGE,{"derivedFrom":sQuery(id+"F0.wireOp",EDGE,"E18.19.5")}),1.0]])]});
            var Q2;
            {var subQ0=sQuery(id+"F0.wireOp",EDGE,"E8");Q2=makeQuery(id+"F0.imprint","IMPRINT",FACE,{"disambiguationData":[TD([[makeQuery(id+"F0.imprint","IMPRINT",EDGE,{"derivedFrom":subQ0}),1.0]])]});}
            var Q3;
            {var subQ0=sQuery(id+"F0.wireOp",EDGE,"E11");Q3=makeQuery(id+"F0.imprint","IMPRINT",FACE,{"disambiguationData":[TD([[makeQuery(id+"F0.imprint","IMPRINT",EDGE,{"derivedFrom":subQ0}),1.0]])]});}
            var Q4;
            {var subQ0=sQuery(id+"F0.wireOp",EDGE,"E18.1.0");Q4=makeQuery(id+"F0.imprint","IMPRINT",FACE,{"disambiguationData":[TD([[makeQuery(id+"F0.imprint","IMPRINT",EDGE,{"derivedFrom":subQ0}),1.0]])]});}
            var Q5;
            Q5=makeQuery(id+"F0.imprint","IMPRINT",FACE,{"disambiguationData":[TD([[makeQuery(id+"F0.imprint","IMPRINT",EDGE,{"derivedFrom":sQuery(id+"F0.wireOp",EDGE,"E18.1.5")}),1.0]])]});
            var Q6;
            {var subQ3=sQuery(id+"F0.wireOp",EDGE,"E18.2.0");Q6=makeQuery(id+"F0.imprint","IMPRINT",FACE,{"disambiguationData":[TD([[makeQuery(id+"F0.imprint","IMPRINT",EDGE,{"derivedFrom":subQ3}),1.0]])]});}
            var Q7;
            Q7=makeQuery(id+"F0.imprint","IMPRINT",FACE,{"disambiguationData":[TD([[makeQuery(id+"F0.imprint","IMPRINT",EDGE,{"derivedFrom":sQuery(id+"F0.wireOp",EDGE,"E18.2.5")}),1.0]])]});
            var Q8;
            {var subQ0=sQuery(id+"F0.wireOp",EDGE,"E18.3.0");Q8=makeQuery(id+"F0.imprint","IMPRINT",FACE,{"disambiguationData":[TD([[makeQuery(id+"F0.imprint","IMPRINT",EDGE,{"derivedFrom":subQ0}),1.0]])]});}
            var Q9;
            Q9=makeQuery(id+"F0.imprint","IMPRINT",FACE,{"disambiguationData":[TD([[makeQuery(id+"F0.imprint","IMPRINT",EDGE,{"derivedFrom":sQuery(id+"F0.wireOp",EDGE,"E18.3.5")}),1.0]])]});
            var Q10;
            {var subQ0=sQuery(id+"F0.wireOp",EDGE,"E18.4.0");Q10=makeQuery(id+"F0.imprint","IMPRINT",FACE,{"disambiguationData":[TD([[makeQuery(id+"F0.imprint","IMPRINT",EDGE,{"derivedFrom":subQ0}),1.0]])]});}
            var Q11;
            Q11=makeQuery(id+"F0.imprint","IMPRINT",FACE,{"disambiguationData":[TD([[makeQuery(id+"F0.imprint","IMPRINT",EDGE,{"derivedFrom":sQuery(id+"F0.wireOp",EDGE,"E18.4.5")}),1.0]])]});
            var Q12;
            {var subQ0=sQuery(id+"F0.wireOp",EDGE,"E18.5.0");Q12=makeQuery(id+"F0.imprint","IMPRINT",FACE,{"disambiguationData":[TD([[makeQuery(id+"F0.imprint","IMPRINT",EDGE,{"derivedFrom":subQ0}),1.0]])]});}
            var Q13;
            Q13=makeQuery(id+"F0.imprint","IMPRINT",FACE,{"disambiguationData":[TD([[makeQuery(id+"F0.imprint","IMPRINT",EDGE,{"derivedFrom":sQuery(id+"F0.wireOp",EDGE,"E18.5.5")}),1.0]])]});
            var Q14;
            {var subQ0=sQuery(id+"F0.wireOp",EDGE,"E18.6.0");Q14=makeQuery(id+"F0.imprint","IMPRINT",FACE,{"disambiguationData":[TD([[makeQuery(id+"F0.imprint","IMPRINT",EDGE,{"derivedFrom":subQ0}),1.0]])]});}
            var Q15;
            Q15=makeQuery(id+"F0.imprint","IMPRINT",FACE,{"disambiguationData":[TD([[makeQuery(id+"F0.imprint","IMPRINT",EDGE,{"derivedFrom":sQuery(id+"F0.wireOp",EDGE,"E18.6.5")}),1.0]])]});
            var Q16;
            {var subQ3=sQuery(id+"F0.wireOp",EDGE,"E18.7.0");Q16=makeQuery(id+"F0.imprint","IMPRINT",FACE,{"disambiguationData":[TD([[makeQuery(id+"F0.imprint","IMPRINT",EDGE,{"derivedFrom":subQ3}),1.0]])]});}
            var Q17;
            Q17=makeQuery(id+"F0.imprint","IMPRINT",FACE,{"disambiguationData":[TD([[makeQuery(id+"F0.imprint","IMPRINT",EDGE,{"derivedFrom":sQuery(id+"F0.wireOp",EDGE,"E18.7.5")}),1.0]])]});
            var Q18;
            {var subQ0=sQuery(id+"F0.wireOp",EDGE,"E18.8.0");Q18=makeQuery(id+"F0.imprint","IMPRINT",FACE,{"disambiguationData":[TD([[makeQuery(id+"F0.imprint","IMPRINT",EDGE,{"derivedFrom":subQ0}),1.0]])]});}
            var Q19;
            Q19=makeQuery(id+"F0.imprint","IMPRINT",FACE,{"disambiguationData":[TD([[makeQuery(id+"F0.imprint","IMPRINT",EDGE,{"derivedFrom":sQuery(id+"F0.wireOp",EDGE,"E18.8.5")}),1.0]])]});
            var Q20;
            {var subQ0=sQuery(id+"F0.wireOp",EDGE,"E18.9.0");Q20=makeQuery(id+"F0.imprint","IMPRINT",FACE,{"disambiguationData":[TD([[makeQuery(id+"F0.imprint","IMPRINT",EDGE,{"derivedFrom":subQ0}),1.0]])]});}
            var Q21;
            Q21=makeQuery(id+"F0.imprint","IMPRINT",FACE,{"disambiguationData":[TD([[makeQuery(id+"F0.imprint","IMPRINT",EDGE,{"derivedFrom":sQuery(id+"F0.wireOp",EDGE,"E18.9.5")}),1.0]])]});
            var Q22;
            {var subQ0=sQuery(id+"F0.wireOp",EDGE,"E18.10.0");Q22=makeQuery(id+"F0.imprint","IMPRINT",FACE,{"disambiguationData":[TD([[makeQuery(id+"F0.imprint","IMPRINT",EDGE,{"derivedFrom":subQ0}),1.0]])]});}
            var Q23;
            Q23=makeQuery(id+"F0.imprint","IMPRINT",FACE,{"disambiguationData":[TD([[makeQuery(id+"F0.imprint","IMPRINT",EDGE,{"derivedFrom":sQuery(id+"F0.wireOp",EDGE,"E18.10.5")}),1.0]])]});
            var Q24;
            {var subQ0=sQuery(id+"F0.wireOp",EDGE,"E18.11.0");Q24=makeQuery(id+"F0.imprint","IMPRINT",FACE,{"disambiguationData":[TD([[makeQuery(id+"F0.imprint","IMPRINT",EDGE,{"derivedFrom":subQ0}),1.0]])]});}
            var Q25;
            Q25=makeQuery(id+"F0.imprint","IMPRINT",FACE,{"disambiguationData":[TD([[makeQuery(id+"F0.imprint","IMPRINT",EDGE,{"derivedFrom":sQuery(id+"F0.wireOp",EDGE,"E18.11.5")}),1.0]])]});
            var Q26;
            {var subQ3=sQuery(id+"F0.wireOp",EDGE,"E18.12.0");Q26=makeQuery(id+"F0.imprint","IMPRINT",FACE,{"disambiguationData":[TD([[makeQuery(id+"F0.imprint","IMPRINT",EDGE,{"derivedFrom":subQ3}),1.0]])]});}
            var Q27;
            Q27=makeQuery(id+"F0.imprint","IMPRINT",FACE,{"disambiguationData":[TD([[makeQuery(id+"F0.imprint","IMPRINT",EDGE,{"derivedFrom":sQuery(id+"F0.wireOp",EDGE,"E18.12.5")}),1.0]])]});
            var Q28;
            {var subQ4=sQuery(id+"F0.wireOp",EDGE,"E18.13.0");Q28=makeQuery(id+"F0.imprint","IMPRINT",FACE,{"disambiguationData":[TD([[makeQuery(id+"F0.imprint","IMPRINT",EDGE,{"derivedFrom":subQ4}),1.0]])]});}
            var Q29;
            Q29=makeQuery(id+"F0.imprint","IMPRINT",FACE,{"disambiguationData":[TD([[makeQuery(id+"F0.imprint","IMPRINT",EDGE,{"derivedFrom":sQuery(id+"F0.wireOp",EDGE,"E18.13.5")}),1.0]])]});
            var Q30;
            {var subQ0=sQuery(id+"F0.wireOp",EDGE,"E18.14.0");Q30=makeQuery(id+"F0.imprint","IMPRINT",FACE,{"disambiguationData":[TD([[makeQuery(id+"F0.imprint","IMPRINT",EDGE,{"derivedFrom":subQ0}),1.0]])]});}
            var Q31;
            Q31=makeQuery(id+"F0.imprint","IMPRINT",FACE,{"disambiguationData":[TD([[makeQuery(id+"F0.imprint","IMPRINT",EDGE,{"derivedFrom":sQuery(id+"F0.wireOp",EDGE,"E18.14.5")}),1.0]])]});
            var Q32;
            {var subQ0=sQuery(id+"F0.wireOp",EDGE,"E18.15.0");Q32=makeQuery(id+"F0.imprint","IMPRINT",FACE,{"disambiguationData":[TD([[makeQuery(id+"F0.imprint","IMPRINT",EDGE,{"derivedFrom":subQ0}),1.0]])]});}
            var Q33;
            Q33=makeQuery(id+"F0.imprint","IMPRINT",FACE,{"disambiguationData":[TD([[makeQuery(id+"F0.imprint","IMPRINT",EDGE,{"derivedFrom":sQuery(id+"F0.wireOp",EDGE,"E18.15.5")}),1.0]])]});
            var Q34;
            {var subQ0=sQuery(id+"F0.wireOp",EDGE,"E18.16.0");Q34=makeQuery(id+"F0.imprint","IMPRINT",FACE,{"disambiguationData":[TD([[makeQuery(id+"F0.imprint","IMPRINT",EDGE,{"derivedFrom":subQ0}),1.0]])]});}
            var Q35;
            Q35=makeQuery(id+"F0.imprint","IMPRINT",FACE,{"disambiguationData":[TD([[makeQuery(id+"F0.imprint","IMPRINT",EDGE,{"derivedFrom":sQuery(id+"F0.wireOp",EDGE,"E18.16.5")}),1.0]])]});
            var Q36;
            {var subQ3=sQuery(id+"F0.wireOp",EDGE,"E18.17.0");Q36=makeQuery(id+"F0.imprint","IMPRINT",FACE,{"disambiguationData":[TD([[makeQuery(id+"F0.imprint","IMPRINT",EDGE,{"derivedFrom":subQ3}),1.0]])]});}
            var Q37;
            Q37=makeQuery(id+"F0.imprint","IMPRINT",FACE,{"disambiguationData":[TD([[makeQuery(id+"F0.imprint","IMPRINT",EDGE,{"derivedFrom":sQuery(id+"F0.wireOp",EDGE,"E18.17.5")}),1.0]])]});
            var Q38;
            {var subQ0=sQuery(id+"F0.wireOp",EDGE,"E18.18.0");Q38=makeQuery(id+"F0.imprint","IMPRINT",FACE,{"disambiguationData":[TD([[makeQuery(id+"F0.imprint","IMPRINT",EDGE,{"derivedFrom":subQ0}),1.0]])]});}
            var Q39;
            Q39=makeQuery(id+"F0.imprint","IMPRINT",FACE,{"disambiguationData":[TD([[makeQuery(id+"F0.imprint","IMPRINT",EDGE,{"derivedFrom":sQuery(id+"F0.wireOp",EDGE,"E18.18.5")}),1.0]])]});
            extrude(context, id + "F4", {"entities" : qUnion([Q0, Q1, Q2, Q3, Q4, Q5, Q6, Q7, Q8, Q9, Q10, Q11, Q12, Q13, Q14, Q15, Q16, Q17, Q18, Q19, Q20, Q21, Q22, Q23, Q24, Q25, Q26, Q27, Q28, Q29, Q30, Q31, Q32, Q33, Q34, Q35, Q36, Q37, Q38, Q39]), "operationType" : NewBodyOperationType.ADD, "depth" : 6 * mm, "offsetDistance" : 25 * mm});
        }
        {
            var Q0;
            {var subQ0=sQuery(id+"F0.wireOp",EDGE,"E7.1.1");Q0=makeQuery(id+"F0.imprint","IMPRINT",FACE,{"disambiguationData":[TD([[makeQuery(id+"F0.imprint","IMPRINT",EDGE,{"derivedFrom":subQ0}),1.0]])]});}
            var Q1;
            {var subQ4=sQuery(id+"F0.wireOp",EDGE,"E7.2.1");Q1=makeQuery(id+"F0.imprint","IMPRINT",FACE,{"disambiguationData":[TD([[makeQuery(id+"F0.imprint","IMPRINT",EDGE,{"derivedFrom":subQ4}),1.0]])]});}
            var Q2;
            {var subQ0=sQuery(id+"F0.wireOp",EDGE,"E7.3.1");Q2=makeQuery(id+"F0.imprint","IMPRINT",FACE,{"disambiguationData":[TD([[makeQuery(id+"F0.imprint","IMPRINT",EDGE,{"derivedFrom":subQ0}),1.0]])]});}
            var Q3;
            {var subQ0=sQuery(id+"F0.wireOp",EDGE,"E7.4.1");Q3=makeQuery(id+"F0.imprint","IMPRINT",FACE,{"disambiguationData":[TD([[makeQuery(id+"F0.imprint","IMPRINT",EDGE,{"derivedFrom":subQ0}),1.0]])]});}
            var Q4;
            {var subQ0=sQuery(id+"F0.wireOp",EDGE,"E7.5.1");Q4=makeQuery(id+"F0.imprint","IMPRINT",FACE,{"disambiguationData":[TD([[makeQuery(id+"F0.imprint","IMPRINT",EDGE,{"derivedFrom":subQ0}),1.0]])]});}
            var Q5;
            {var subQ0=sQuery(id+"F0.wireOp",EDGE,"E7.6.1");Q5=makeQuery(id+"F0.imprint","IMPRINT",FACE,{"disambiguationData":[TD([[makeQuery(id+"F0.imprint","IMPRINT",EDGE,{"derivedFrom":subQ0}),1.0]])]});}
            var Q6;
            {var subQ6=sQuery(id+"F0.wireOp",EDGE,"E7.7.1");Q6=makeQuery(id+"F0.imprint","IMPRINT",FACE,{"disambiguationData":[TD([[makeQuery(id+"F0.imprint","IMPRINT",EDGE,{"derivedFrom":subQ6}),1.0]])]});}
            var Q7;
            {var subQ0=sQuery(id+"F0.wireOp",EDGE,"E7.8.1");Q7=makeQuery(id+"F0.imprint","IMPRINT",FACE,{"disambiguationData":[TD([[makeQuery(id+"F0.imprint","IMPRINT",EDGE,{"derivedFrom":subQ0}),1.0]])]});}
            var Q8;
            {var subQ0=sQuery(id+"F0.wireOp",EDGE,"E7.9.1");Q8=makeQuery(id+"F0.imprint","IMPRINT",FACE,{"disambiguationData":[TD([[makeQuery(id+"F0.imprint","IMPRINT",EDGE,{"derivedFrom":subQ0}),1.0]])]});}
            var Q9;
            {var subQ0=sQuery(id+"F0.wireOp",EDGE,"E7.10.1");Q9=makeQuery(id+"F0.imprint","IMPRINT",FACE,{"disambiguationData":[TD([[makeQuery(id+"F0.imprint","IMPRINT",EDGE,{"derivedFrom":subQ0}),1.0]])]});}
            var Q10;
            {var subQ0=sQuery(id+"F0.wireOp",EDGE,"E7.11.1");Q10=makeQuery(id+"F0.imprint","IMPRINT",FACE,{"disambiguationData":[TD([[makeQuery(id+"F0.imprint","IMPRINT",EDGE,{"derivedFrom":subQ0}),1.0]])]});}
            var Q11;
            {var subQ4=sQuery(id+"F0.wireOp",EDGE,"E7.12.1");Q11=makeQuery(id+"F0.imprint","IMPRINT",FACE,{"disambiguationData":[TD([[makeQuery(id+"F0.imprint","IMPRINT",EDGE,{"derivedFrom":subQ4}),1.0]])]});}
            var Q12;
            {var subQ0=sQuery(id+"F0.wireOp",EDGE,"E7.13.1");Q12=makeQuery(id+"F0.imprint","IMPRINT",FACE,{"disambiguationData":[TD([[makeQuery(id+"F0.imprint","IMPRINT",EDGE,{"derivedFrom":subQ0}),1.0]])]});}
            var Q13;
            {var subQ0=sQuery(id+"F0.wireOp",EDGE,"E7.14.1");Q13=makeQuery(id+"F0.imprint","IMPRINT",FACE,{"disambiguationData":[TD([[makeQuery(id+"F0.imprint","IMPRINT",EDGE,{"derivedFrom":subQ0}),1.0]])]});}
            var Q14;
            {var subQ0=sQuery(id+"F0.wireOp",EDGE,"E7.15.1");Q14=makeQuery(id+"F0.imprint","IMPRINT",FACE,{"disambiguationData":[TD([[makeQuery(id+"F0.imprint","IMPRINT",EDGE,{"derivedFrom":subQ0}),1.0]])]});}
            var Q15;
            {var subQ0=sQuery(id+"F0.wireOp",EDGE,"E7.16.1");Q15=makeQuery(id+"F0.imprint","IMPRINT",FACE,{"disambiguationData":[TD([[makeQuery(id+"F0.imprint","IMPRINT",EDGE,{"derivedFrom":subQ0}),1.0]])]});}
            var Q16;
            {var subQ4=sQuery(id+"F0.wireOp",EDGE,"E7.17.1");Q16=makeQuery(id+"F0.imprint","IMPRINT",FACE,{"disambiguationData":[TD([[makeQuery(id+"F0.imprint","IMPRINT",EDGE,{"derivedFrom":subQ4}),1.0]])]});}
            var Q17;
            {var subQ0=sQuery(id+"F0.wireOp",EDGE,"E7.18.1");Q17=makeQuery(id+"F0.imprint","IMPRINT",FACE,{"disambiguationData":[TD([[makeQuery(id+"F0.imprint","IMPRINT",EDGE,{"derivedFrom":subQ0}),1.0]])]});}
            var Q18;
            {var subQ0=sQuery(id+"F0.wireOp",EDGE,"E7.19.1");Q18=makeQuery(id+"F0.imprint","IMPRINT",FACE,{"disambiguationData":[TD([[makeQuery(id+"F0.imprint","IMPRINT",EDGE,{"derivedFrom":subQ0}),1.0]])]});}
            var Q19;
            {var subQ0=sQuery(id+"F0.wireOp",EDGE,"E4");Q19=makeQuery(id+"F0.imprint","IMPRINT",FACE,{"disambiguationData":[TD([[makeQuery(id+"F0.imprint","IMPRINT",EDGE,{"derivedFrom":subQ0}),1.0]])]});}
            extrude(context, id + "F5", {"entities" : qUnion([Q0, Q1, Q2, Q3, Q4, Q5, Q6, Q7, Q8, Q9, Q10, Q11, Q12, Q13, Q14, Q15, Q16, Q17, Q18, Q19]), "operationType" : NewBodyOperationType.ADD, "depth" : 9 * mm, "offsetDistance" : 25 * mm});
        }
        {
            var Q0;
            Q0=qCreatedBy(makeId("Top.planeOp"),FACE);
            var sketch = newSketch(context, id + "F6", { "sketchPlane" : qUnion([Q0])});
            skText(sketch, "E19", { "text": "LANGLOIS LAB", "fontName": "OpenSans-Regular.ttf"});
            const initialGuessF6  = {"E19": [0.0387, -0.01044, 1, 0, 0.02088]};
            skSetInitialGuess(sketch, initialGuessF6);
            skSolve(sketch);
        }
        {
            var Q0;
            Q0 = qSketchRegion(id + "F6", true);
            extrude(context, id + "F7", {"entities" : qUnion([Q0]), "depth" : 9 * mm, "offsetDistance" : 25 * mm});
        }
        {
            var Q0;
            Q0=qCreatedBy(makeId("Top.planeOp"),FACE);
            cPlane(context, id + "F8", {"entities" : qUnion([Q0]), "cplaneType" : CPlaneType.OFFSET, "offset" : 5 * mm, "oppositeDirection" : true, "width" : 150 * mm, "height" : 150 * mm});
        }
        {
            var Q0;
            Q0=qCreatedBy(id+"F8.planeOp",FACE);
            var sketch = newSketch(context, id + "F9", { "sketchPlane" : qUnion([Q0])});
            skLineSegment(sketch, "E20.bottom", {"start": v(-37.18, -37.16) * mm, "end": v(239.27, -37.16) * mm});
            skLineSegment(sketch, "E20.top", {"start": v(-37.18, 41.29) * mm, "end": v(239.27, 41.29) * mm});
            skLineSegment(sketch, "E20.left", {"start": v(-37.18, -37.16) * mm, "end": v(-37.18, 41.29) * mm});
            skLineSegment(sketch, "E20.right", {"start": v(239.27, -37.16) * mm, "end": v(239.27, 41.29) * mm});
            skSolve(sketch);
        }
        {
            var Q0;
            Q0 = qSketchRegion(id + "F9", true);
            extrude(context, id + "F10", {"entities" : qUnion([Q0]), "operationType" : NewBodyOperationType.ADD, "depth" : 5 * mm, "offsetDistance" : 25 * mm});
        }
    });
